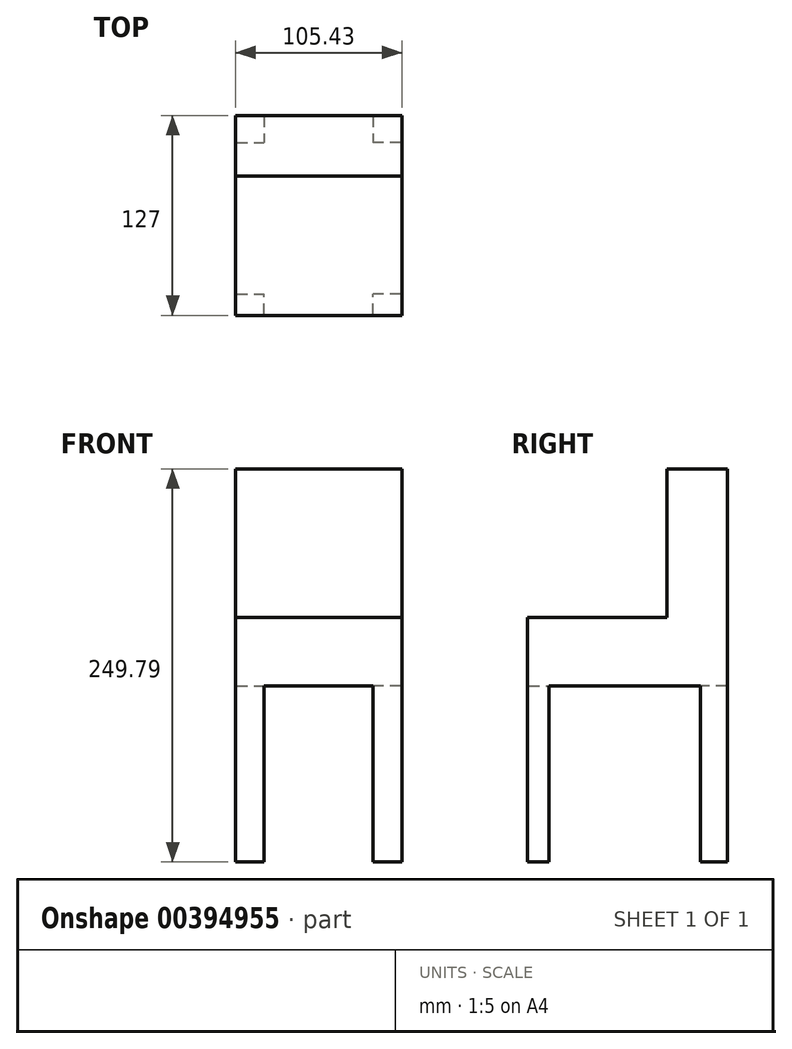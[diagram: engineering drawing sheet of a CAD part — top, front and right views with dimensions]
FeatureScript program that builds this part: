
annotation { "Feature Type Name" : "Feature", "Feature Type Description" : "" }
export const myFeature = defineFeature(function(context is Context, id is Id, definition is map)
    precondition{}
    {
        {
            var Q0;
            Q0=qCreatedBy(makeId("Front.planeOp"),FACE);
            var sketch = newSketch(context, id + "F0", { "sketchPlane" : qUnion([Q0])});
            skLineSegment(sketch, "E0.bottom", {"start": v(-72.02, 16.9) * mm, "end": v(33.41, 16.9) * mm});
            skLineSegment(sketch, "E0.top", {"start": v(-72.02, -51.8) * mm, "end": v(33.41, -51.8) * mm});
            skLineSegment(sketch, "E0.left", {"start": v(-72.02, 16.9) * mm, "end": v(-72.02, -51.8) * mm});
            skLineSegment(sketch, "E0.right", {"start": v(33.41, 16.9) * mm, "end": v(33.41, -51.8) * mm});
            skSolve(sketch);
        }
        {
            var Q0;
            Q0=makeQuery(id+"F0.imprint","IMPRINT",FACE,{"disambiguationData":[TD([[makeQuery(id+"F0.imprint","IMPRINT",EDGE,{"derivedFrom":sQuery(id+"F0.wireOp",EDGE,"E0.bottom")}),-1.0]])]});
            extrude(context, id + "F1", {"entities" : qUnion([Q0]), "depth" : 127 * mm});
        }
        {
            var Q0;
            Q0=makeQuery(id+"F1.opExtrude","SWEPT_FACE",FACE,{"disambiguationData":[OSD([sQuery(id+"F0.wireOp",EDGE,"E0.bottom")])]});
            extrude(context, id + "F2", {"entities" : qUnion([Q0]), "operationType" : NewBodyOperationType.REMOVE, "oppositeDirection" : true, "depth" : 25.4 * mm});
        }
        {
            var Q0;
            Q0=makeQuery(id+"F2.boolean.opBoolean","COPY",FACE,{"derivedFrom":makeQuery(id+"F2.opExtrude","CAP_FACE",FACE,{"disambiguationData":[OSD([sQuery(id+"F0.wireOp",EDGE,"E0.bottom")])],"isStart":false})});
            var sketch = newSketch(context, id + "F3", { "sketchPlane" : qUnion([Q0])});
            skLineSegment(sketch, "E1.bottom", {"start": v(33.41, 0) * mm, "end": v(-72.02, 0) * mm});
            skLineSegment(sketch, "E1.top", {"start": v(33.41, -38.42) * mm, "end": v(-72.02, -38.42) * mm});
            skLineSegment(sketch, "E1.left", {"start": v(33.41, 0) * mm, "end": v(33.41, -38.42) * mm});
            skLineSegment(sketch, "E1.right", {"start": v(-72.02, 0) * mm, "end": v(-72.02, -38.42) * mm});
            skSolve(sketch);
        }
        {
            var Q0;
            Q0 = qSketchRegion(id + "F3", true);
            extrude(context, id + "F4", {"entities" : qUnion([Q0]), "operationType" : NewBodyOperationType.ADD, "depth" : 94.49 * mm});
        }
        {
            var Q0;
            Q0=makeQuery(id+"F1.opExtrude","SWEPT_FACE",FACE,{"disambiguationData":[OSD([sQuery(id+"F0.wireOp",EDGE,"E0.top")])]});
            var sketch = newSketch(context, id + "F5", { "sketchPlane" : qUnion([Q0])});
            skLineSegment(sketch, "E2.bottom", {"start": v(-72.02, 0) * mm, "end": v(-53.93, 0) * mm});
            skLineSegment(sketch, "E2.top", {"start": v(-72.02, 17.2) * mm, "end": v(-53.93, 17.2) * mm});
            skLineSegment(sketch, "E2.left", {"start": v(-72.02, 0) * mm, "end": v(-72.02, 17.2) * mm});
            skLineSegment(sketch, "E2.right", {"start": v(-53.93, 0) * mm, "end": v(-53.93, 17.2) * mm});
            skLineSegment(sketch, "E3.bottom", {"start": v(33.41, 0) * mm, "end": v(15, 0) * mm});
            skLineSegment(sketch, "E3.top", {"start": v(33.41, 17.2) * mm, "end": v(15, 17.2) * mm});
            skLineSegment(sketch, "E3.left", {"start": v(33.41, 0) * mm, "end": v(33.41, 17.2) * mm});
            skLineSegment(sketch, "E3.right", {"start": v(15, 0) * mm, "end": v(15, 17.2) * mm});
            skLineSegment(sketch, "E4.bottom", {"start": v(33.41, 127) * mm, "end": v(15, 127) * mm});
            skLineSegment(sketch, "E4.top", {"start": v(33.41, 113.6) * mm, "end": v(15, 113.6) * mm});
            skLineSegment(sketch, "E4.left", {"start": v(33.41, 127) * mm, "end": v(33.41, 113.6) * mm});
            skLineSegment(sketch, "E4.right", {"start": v(15, 127) * mm, "end": v(15, 113.6) * mm});
            skLineSegment(sketch, "E5.bottom", {"start": v(-72.02, 127) * mm, "end": v(-53.93, 127) * mm});
            skLineSegment(sketch, "E5.top", {"start": v(-72.02, 113.6) * mm, "end": v(-53.93, 113.6) * mm});
            skLineSegment(sketch, "E5.left", {"start": v(-72.02, 127) * mm, "end": v(-72.02, 113.6) * mm});
            skLineSegment(sketch, "E5.right", {"start": v(-53.93, 127) * mm, "end": v(-53.93, 113.6) * mm});
            skSolve(sketch);
        }
        {
            var Q0;
            Q0 = qSketchRegion(id + "F5", true);
            extrude(context, id + "F6", {"entities" : qUnion([Q0]), "operationType" : NewBodyOperationType.ADD, "depth" : 112.01 * mm});
        }
    });
